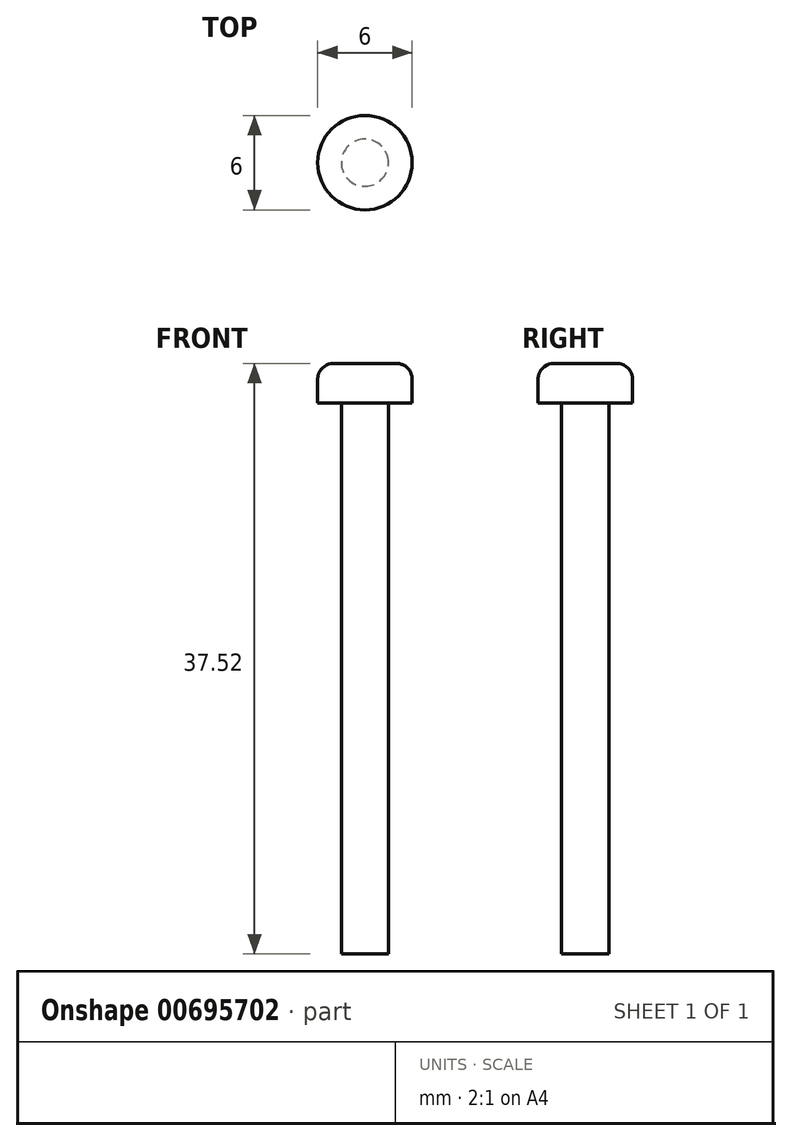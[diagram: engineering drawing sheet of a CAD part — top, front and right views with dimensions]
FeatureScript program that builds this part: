
annotation { "Feature Type Name" : "Feature", "Feature Type Description" : "" }
export const myFeature = defineFeature(function(context is Context, id is Id, definition is map)
    precondition{}
    {
        {
            var Q0;
            Q0=qCreatedBy(makeId("Top.planeOp"),FACE);
            var sketch = newSketch(context, id + "F0", { "sketchPlane" : qUnion([Q0])});
            skCircle(sketch, "E0", {"center": v(0, 0) * mm, "radius": 1.5 * mm});
            skSolve(sketch);
        }
        {
            var Q0;
            Q0=qCreatedBy(makeId("Top.planeOp"),FACE);
            var sketch = newSketch(context, id + "F1", { "sketchPlane" : qUnion([Q0])});
            skCircle(sketch, "E1", {"center": v(0, 0) * mm, "radius": 3 * mm});
            skSolve(sketch);
        }
        {
            var Q0;
            Q0 = qSketchRegion(id + "F0", true);
            extrude(context, id + "F2", {"entities" : qUnion([Q0]), "oppositeDirection" : true, "depth" : 35 * mm, "offsetDistance" : 25 * mm});
        }
        {
            var Q0;
            Q0 = qSketchRegion(id + "F1", true);
            extrude(context, id + "F3", {"entities" : qUnion([Q0]), "operationType" : NewBodyOperationType.ADD, "depth" : 2.52 * mm, "offsetDistance" : 25 * mm});
        }
        {
            var Q0;
            Q0=makeQuery(id+"F3.opExtrude","CAP_FACE",FACE,{"disambiguationData":[OSD([sQuery(id+"F1.wireOp",EDGE,"E1")])],"isStart":false});
            fillet(context, id + "F4", {"entities" : qUnion([Q0]), "radius" : 1 * mm, "tangentPropagation" : true, "allowEdgeOverflow" : false});
        }
    });
